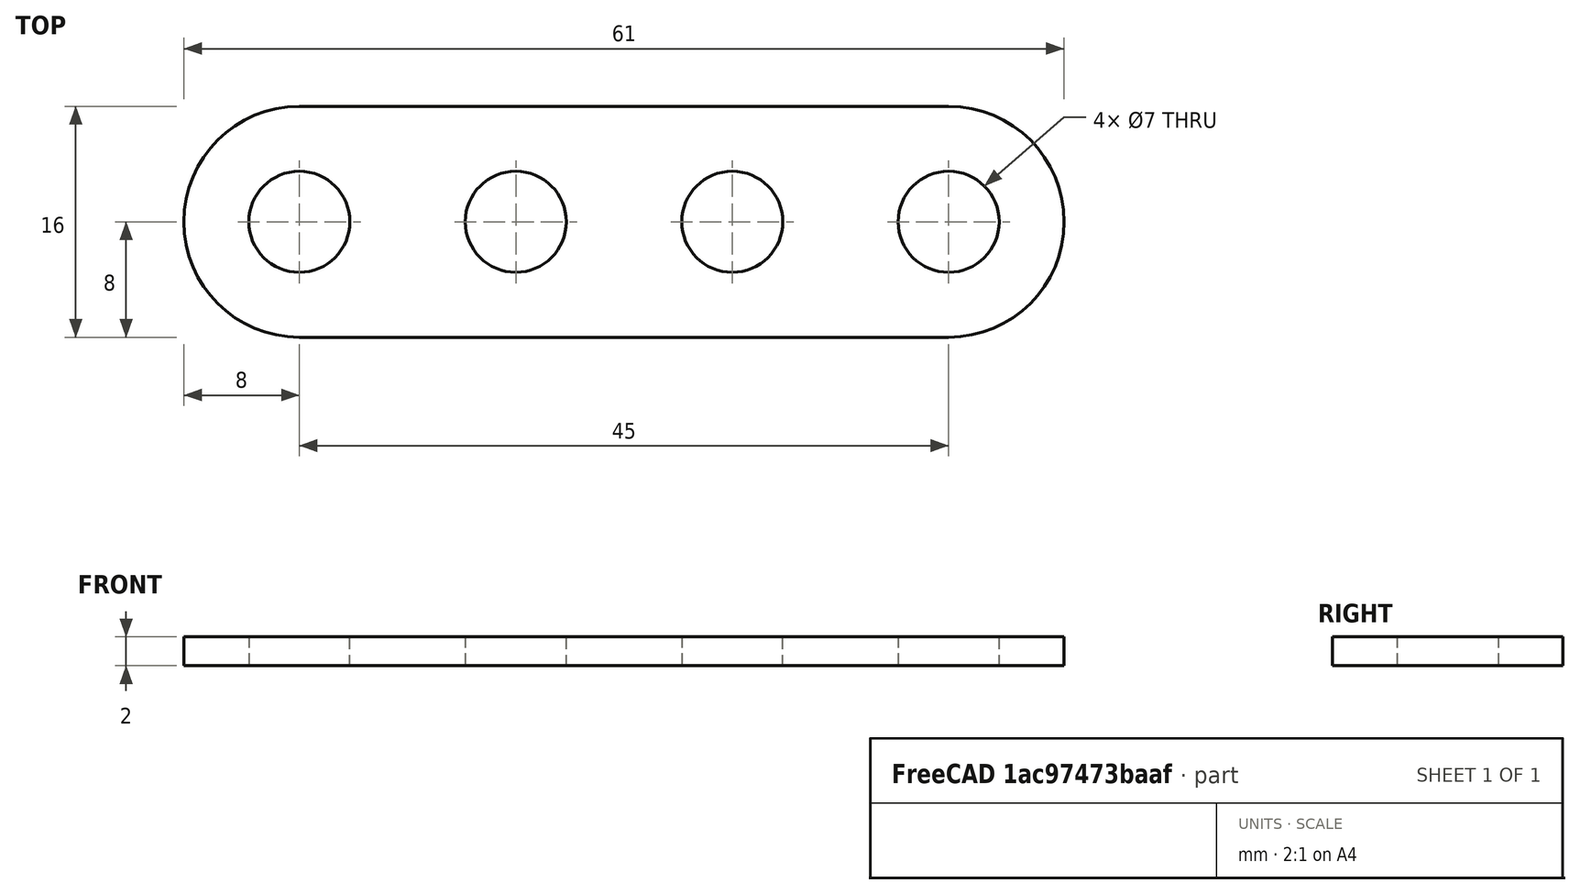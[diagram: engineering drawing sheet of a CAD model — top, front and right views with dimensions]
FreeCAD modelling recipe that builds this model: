
FCSTD DOCUMENT  (FreeCAD 0.19R24291 (Git))
Label: door opener tie 1
License: All rights reserved
LicenseURL: http://en.wikipedia.org/wiki/All_rights_reserved
objects: Sketcher::SketchObject×1, PartDesign::Pad×1, PartDesign::Body×1
note: 4 computed .brp shape members not serialized (recipe doc carries the construction recipe); baked Part::Feature solids carry a one-line shape summary decoded from their .brp

FEATURE [Sketcher::SketchObject] Sketch
  FullyConstrained = true
  MapMode = 5
  Support = -> [XY_Plane]
  sketch-geometry (11):
    g0: ArcOfCircle CenterX=-22.5 CenterY=-1e-16 CenterZ=0 NormalX=0 NormalY=0 NormalZ=1 AngleXU=0 Radius=8 StartAngle=1.5708 EndAngle=4.71239
    g1: ArcOfCircle CenterX=22.5 CenterY=1e-16 CenterZ=0 NormalX=0 NormalY=0 NormalZ=1 AngleXU=0 Radius=8 StartAngle=4.71239 EndAngle=7.85398
    g2: LineSegment StartX=-22.5 StartY=-8 StartZ=0 EndX=22.5 EndY=-8 EndZ=0
    g3: LineSegment StartX=-22.5 StartY=8 StartZ=0 EndX=22.5 EndY=8 EndZ=0
    g4: Circle CenterX=-22.5 CenterY=0 CenterZ=0 NormalX=0 NormalY=0 NormalZ=1 AngleXU=0 Radius=3.5
    g5: Circle CenterX=22.5 CenterY=0 CenterZ=0 NormalX=0 NormalY=0 NormalZ=1 AngleXU=0 Radius=3.5
    g6: Circle CenterX=-7.5 CenterY=0 CenterZ=0 NormalX=0 NormalY=0 NormalZ=1 AngleXU=0 Radius=3.5
    g7: Circle CenterX=7.5 CenterY=0 CenterZ=0 NormalX=0 NormalY=0 NormalZ=1 AngleXU=0 Radius=3.5
    g8: LineSegment StartX=-22.5 StartY=-1e-16 StartZ=0 EndX=-7.5 EndY=0 EndZ=0
    g9: LineSegment StartX=-7.5 StartY=0 StartZ=0 EndX=7.5 EndY=0 EndZ=0
    g10: LineSegment StartX=7.5 StartY=0 StartZ=0 EndX=22.5 EndY=1e-16 EndZ=0
  constraints (25):
    c: Tangent(g0,g3) = 1.5708
    c: Tangent(g0,g2) = -1.5708
    c: Tangent(g2,g1) = -1.5708
    c: Tangent(g3,g1) = 1.5708
    c: Horizontal(g2)
    c: Equal(g0,g1)
    c: Symmetric(g0,g1,g-1)
    c: PointOnObject(g4,g-1)
    c: Equal(g5,g4)
    c: Symmetric(g4,g5,g-1)
    c: Diameter(g4) = 7
    c: Vertical(g0,g4)
    c: DistanceY(g0,g0) = 8
    c: Equal(g4,g6)
    c: Equal(g6,g7)
    c: PointOnObject(g6,g-1)
    c: Symmetric(g6,g7,g-1)
    c: Coincident(g8,g0)
    c: Coincident(g8,g6)
    c: Coincident(g9,g6)
    c: Coincident(g9,g7)
    c: Coincident(g10,g7)
    c: Coincident(g10,g1)
    c: Equal(g8,g9)
    c: DistanceX(g6,g7) = 15
FEATURE [PartDesign::Pad] Pad
  Direction = (1,1,1)
  Length = 2
  Length2 = 100
  Profile = -> Sketch
  Type = 0
FEATURE [PartDesign::Body] Body
  Group = -> [Sketch,Pad]
  Origin = -> Origin
  Tip = -> Pad
